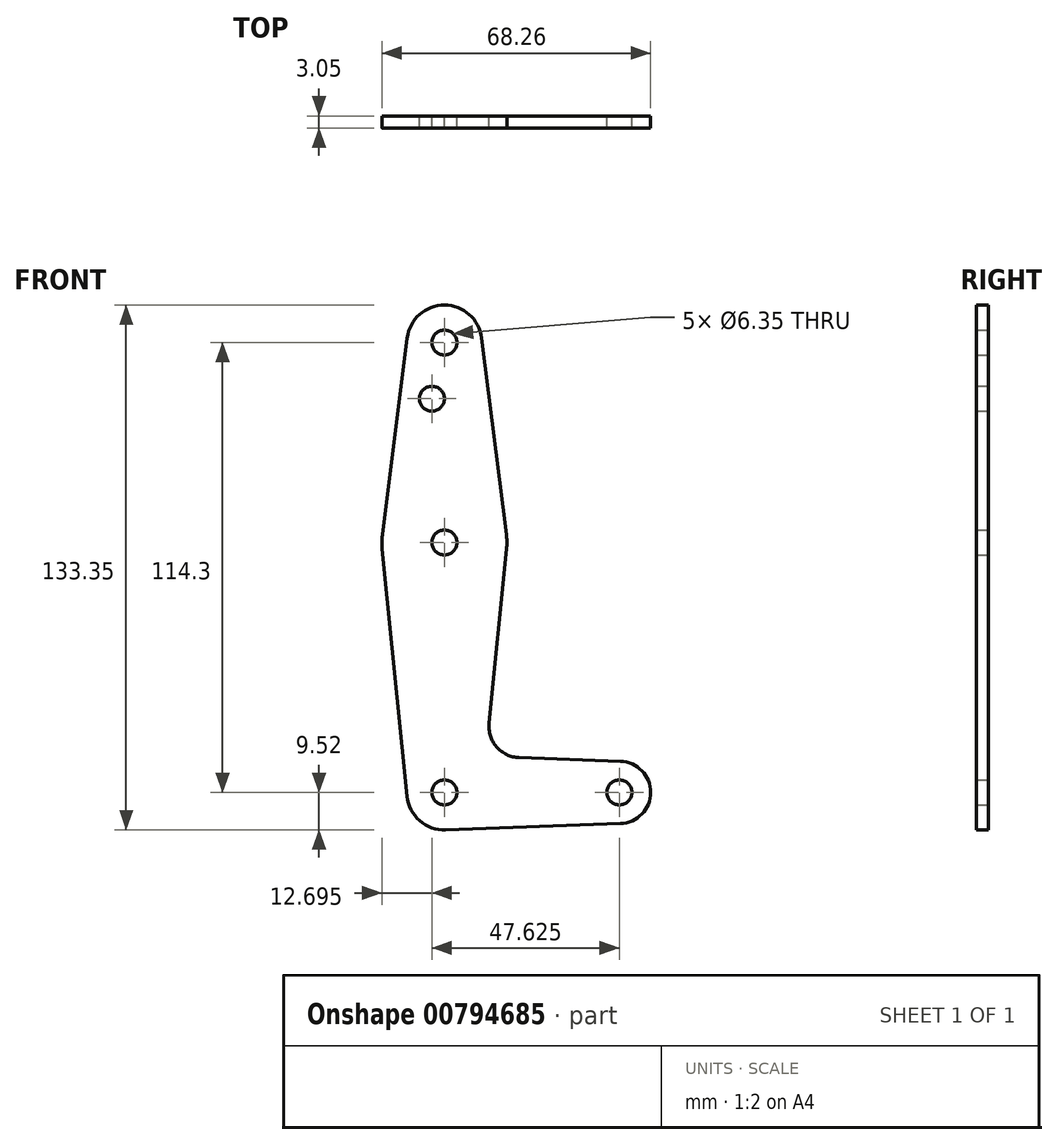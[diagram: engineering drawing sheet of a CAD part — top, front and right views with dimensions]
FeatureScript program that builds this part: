
annotation { "Feature Type Name" : "Feature", "Feature Type Description" : "" }
export const myFeature = defineFeature(function(context is Context, id is Id, definition is map)
    precondition{}
    {
        {
            var Q0;
            Q0=qCreatedBy(makeId("Front.planeOp"),FACE);
            var sketch = newSketch(context, id + "F0", { "sketchPlane" : qUnion([Q0])});
            skCircle(sketch, "E0", {"center": v(0, 0) * mm, "radius": 9.53 * mm});
            skCircle(sketch, "E1", {"center": v(0, 63.5) * mm, "radius": 15.88 * mm});
            skCircle(sketch, "E2", {"center": v(0, 114.3) * mm, "radius": 9.53 * mm});
            skCircle(sketch, "E3", {"center": v(44.45, 0) * mm, "radius": 7.94 * mm});
            skLineSegment(sketch, "E4", {"start": v(0, 114.3) * mm, "end": v(0, 0) * mm, "construction": true});
            skLineSegment(sketch, "E5", {"start": v(44.45, 0) * mm, "end": v(0, 0) * mm, "construction": true});
            skLineSegment(sketch, "E6", {"start": v(-9.45, 115.5) * mm, "end": v(-15.75, 65.48) * mm});
            skLineSegment(sketch, "E7", {"start": v(-15.8, 61.91) * mm, "end": v(-9.48, -0.95) * mm});
            skLineSegment(sketch, "E8", {"start": v(11.34, 17.6) * mm, "end": v(15.8, 61.91) * mm});
            skLineSegment(sketch, "E9", {"start": v(15.75, 65.48) * mm, "end": v(9.45, 115.5) * mm});
            skCircle(sketch, "E10", {"center": v(0, 114.3) * mm, "radius": 3.18 * mm});
            skCircle(sketch, "E11", {"center": v(-3.17, 100.03) * mm, "radius": 3.18 * mm});
            skCircle(sketch, "E12", {"center": v(0, 63.5) * mm, "radius": 3.18 * mm});
            skCircle(sketch, "E13", {"center": v(0, 0) * mm, "radius": 3.18 * mm});
            skCircle(sketch, "E14", {"center": v(44.45, 0) * mm, "radius": 3.18 * mm});
            skLineSegment(sketch, "E15", {"start": v(18.97, 8.85) * mm, "end": v(44.73, 7.93) * mm});
            skLineSegment(sketch, "E16", {"start": v(0.34, -9.52) * mm, "end": v(44.73, -7.93) * mm});
            skArc(sketch, "E17.filletArc", {"start": v(11.34, 17.6) * mm, "mid": v(13.26, 11.57) * mm, "end": v(18.97, 8.85) * mm});
            skSolve(sketch);
        }
        {
            var Q0;
            Q0 = qSketchRegion(id + "F0", true);
            extrude(context, id + "F1", {"entities" : qUnion([Q0]), "depth" : 3.05 * mm, "offsetDistance" : 25.4 * mm});
        }
    });
